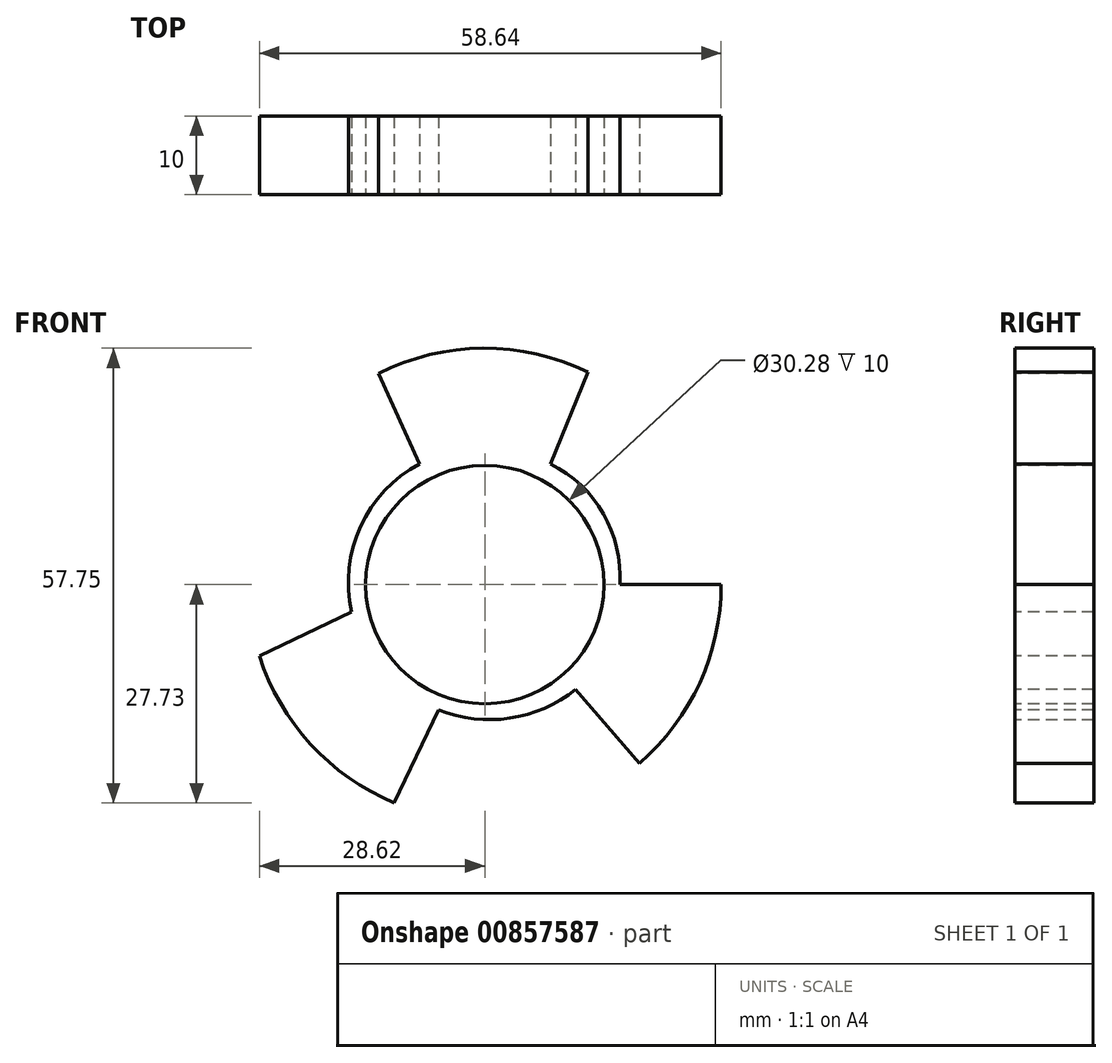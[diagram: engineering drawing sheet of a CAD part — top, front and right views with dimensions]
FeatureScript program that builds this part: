
annotation { "Feature Type Name" : "Feature", "Feature Type Description" : "" }
export const myFeature = defineFeature(function(context is Context, id is Id, definition is map)
    precondition{}
    {
        {
            var Q0;
            Q0=qCreatedBy(makeId("Front.planeOp"),FACE);
            var sketch = newSketch(context, id + "F0", { "sketchPlane" : qUnion([Q0])});
            skCircle(sketch, "E0", {"center": v(0, 0) * mm, "radius": 30.02 * mm});
            skSolve(sketch);
        }
        {
            var Q0;
            Q0=makeQuery(id+"F0.imprint","IMPRINT",FACE,{"disambiguationData":[TD([[makeQuery(id+"F0.imprint","IMPRINT",EDGE,{"derivedFrom":sQuery(id+"F0.wireOp",EDGE,"E0")}),1.0]])]});
            extrude(context, id + "F1", {"entities" : qUnion([Q0]), "depth" : 10 * mm, "offsetDistance" : 25 * mm});
        }
        {
            var Q0;
            Q0=makeQuery(id+"F1.opExtrude","CAP_FACE",FACE,{"disambiguationData":[OSD([sQuery(id+"F0.wireOp",EDGE,"E0")])],"isStart":false});
            var sketch = newSketch(context, id + "F2", { "sketchPlane" : qUnion([Q0])});
            skLineSegment(sketch, "E1", {"start": v(13.12, 27) * mm, "end": v(8.34, 15.33) * mm});
            skLineSegment(sketch, "E2", {"start": v(-13.52, 26.8) * mm, "end": v(-8.29, 15.33) * mm});
            skLineSegment(sketch, "E3", {"start": v(-28.62, -9.07) * mm, "end": v(-16.9, -3.5) * mm});
            skLineSegment(sketch, "E4", {"start": v(-5.89, -15.92) * mm, "end": v(-11.5, -27.73) * mm});
            skLineSegment(sketch, "E5", {"start": v(30.02, 0) * mm, "end": v(17.15, 0) * mm});
            skLineSegment(sketch, "E6", {"start": v(19.66, -22.69) * mm, "end": v(11.54, -13.31) * mm});
            skArc(sketch, "E7", {"start": v(13.12, 27) * mm, "mid": v(-0.23, 30.34) * mm, "end": v(-13.52, 26.8) * mm});
            skArc(sketch, "E8", {"start": v(19.66, -22.69) * mm, "mid": v(27.43, -12.52) * mm, "end": v(30.02, 0) * mm});
            skArc(sketch, "E9", {"start": v(-28.62, -9.07) * mm, "mid": v(-22.57, -20.7) * mm, "end": v(-11.5, -27.73) * mm});
            skArc(sketch, "E10", {"start": v(-8.29, 15.33) * mm, "mid": v(-15.78, 7.37) * mm, "end": v(-16.9, -3.5) * mm});
            skArc(sketch, "E11", {"start": v(17.15, 0) * mm, "mid": v(15.05, 9) * mm, "end": v(8.34, 15.33) * mm});
            skArc(sketch, "E12", {"start": v(-5.89, -15.92) * mm, "mid": v(3.18, -16.97) * mm, "end": v(11.54, -13.31) * mm});
            skSolve(sketch);
        }
        {
            var Q0;
            {var subQ0=sQuery(id+"F2.wireOp",EDGE,"E7");Q0=makeQuery(id+"F2.imprint","IMPRINT",FACE,{"disambiguationData":[TD([[makeQuery(id+"F2.imprint","IMPRINT",EDGE,{"derivedFrom":subQ0}),1.0]])]});}
            var Q1;
            {var subQ0=sQuery(id+"F2.wireOp",EDGE,"E8");Q1=makeQuery(id+"F2.imprint","IMPRINT",FACE,{"disambiguationData":[TD([[makeQuery(id+"F2.imprint","IMPRINT",EDGE,{"derivedFrom":subQ0}),1.0]])]});}
            var Q2;
            {var subQ0=sQuery(id+"F2.wireOp",EDGE,"E9");Q2=makeQuery(id+"F2.imprint","IMPRINT",FACE,{"disambiguationData":[TD([[makeQuery(id+"F2.imprint","IMPRINT",EDGE,{"derivedFrom":subQ0}),1.0]])]});}
            var Q3;
            {var subQ0=sQuery(id+"F2.wireOp",EDGE,"E2");Q3=makeQuery(id+"F2.imprint","IMPRINT",FACE,{"disambiguationData":[TD([[makeQuery(id+"F2.imprint","IMPRINT",EDGE,{"derivedFrom":subQ0}),-1.0]])]});}
            var Q4;
            {var subQ0=sQuery(id+"F2.wireOp",EDGE,"E4");Q4=makeQuery(id+"F2.imprint","IMPRINT",FACE,{"disambiguationData":[TD([[makeQuery(id+"F2.imprint","IMPRINT",EDGE,{"derivedFrom":subQ0}),1.0]])]});}
            var Q5;
            {var subQ0=sQuery(id+"F2.wireOp",EDGE,"E1");Q5=makeQuery(id+"F2.imprint","IMPRINT",FACE,{"disambiguationData":[TD([[makeQuery(id+"F2.imprint","IMPRINT",EDGE,{"derivedFrom":subQ0}),1.0]])]});}
            extrude(context, id + "F3", {"entities" : qUnion([Q0, Q1, Q2, Q3, Q4, Q5]), "operationType" : NewBodyOperationType.REMOVE, "oppositeDirection" : true, "depth" : 25 * mm, "offsetDistance" : 25 * mm});
        }
        {
            var Q0;
            Q0=makeQuery(id+"F1.opExtrude","CAP_FACE",FACE,{"disambiguationData":[OSD([sQuery(id+"F0.wireOp",EDGE,"E0")])],"isStart":false});
            var sketch = newSketch(context, id + "F4", { "sketchPlane" : qUnion([Q0])});
            skCircle(sketch, "E13", {"center": v(0, 0) * mm, "radius": 15.14 * mm});
            skSolve(sketch);
        }
        {
            var Q0;
            Q0=makeQuery(id+"F4.imprint","IMPRINT",FACE,{"disambiguationData":[TD([[makeQuery(id+"F4.imprint","IMPRINT",EDGE,{"derivedFrom":sQuery(id+"F4.wireOp",EDGE,"E13")}),1.0]])]});
            extrude(context, id + "F5", {"entities" : qUnion([Q0]), "operationType" : NewBodyOperationType.REMOVE, "oppositeDirection" : true, "depth" : 25 * mm, "offsetDistance" : 25 * mm});
        }
    });
